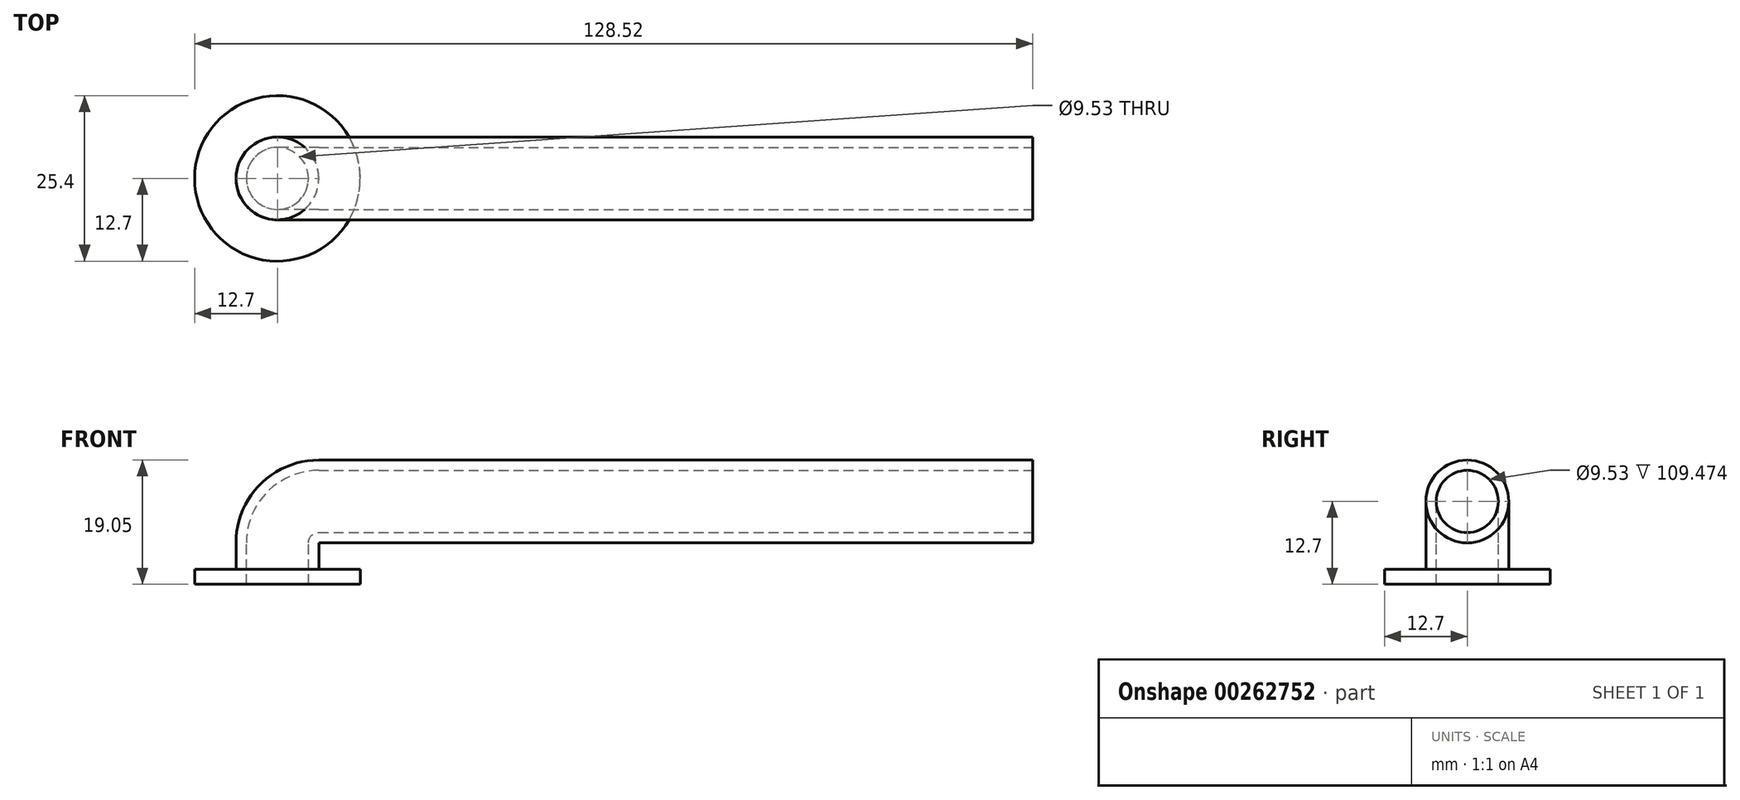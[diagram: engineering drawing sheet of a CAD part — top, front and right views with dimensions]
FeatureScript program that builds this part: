
annotation { "Feature Type Name" : "Feature", "Feature Type Description" : "" }
export const myFeature = defineFeature(function(context is Context, id is Id, definition is map)
    precondition{}
    {
        {
            var Q0;
            Q0=qCreatedBy(makeId("Front.planeOp"),FACE);
            var sketch = newSketch(context, id + "F0", { "sketchPlane" : qUnion([Q0])});
            skLineSegment(sketch, "E0", {"start": v(0, 0) * mm, "end": v(0, 6.35) * mm});
            skLineSegment(sketch, "E1", {"start": v(6.35, 12.7) * mm, "end": v(115.82, 12.7) * mm});
            skPoint(sketch, "E2.visualSharp", {"position": v(0, 12.7) * mm});
            skArc(sketch, "E2.filletArc", {"start": v(6.35, 12.7) * mm, "mid": v(1.86, 10.84) * mm, "end": v(0, 6.35) * mm});
            skSolve(sketch);
        }
        {
            var Q0;
            Q0=qCreatedBy(makeId("Top.planeOp"),FACE);
            var sketch = newSketch(context, id + "F1", { "sketchPlane" : qUnion([Q0])});
            skCircle(sketch, "E3", {"center": v(0, 0) * mm, "radius": 6.35 * mm});
            skCircle(sketch, "E4", {"center": v(0, 0) * mm, "radius": 4.76 * mm});
            skSolve(sketch);
        }
        {
            var Q0;
            Q0=makeQuery(id+"F1.imprint","IMPRINT",FACE,{"disambiguationData":[TD([[makeQuery(id+"F1.imprint","IMPRINT",EDGE,{"derivedFrom":sQuery(id+"F1.wireOp",EDGE,"E3")}),1.0]])]});
            var Q1;
            Q1=sQuery(id+"F0.wireOp",EDGE,"E1");
            var Q2;
            Q2=sQuery(id+"F0.wireOp",EDGE,"E2.filletArc");
            var Q3;
            Q3=sQuery(id+"F0.wireOp",EDGE,"E0");
            sweep(context, id + "F2", {"profiles" : qUnion([Q0]), "path" : qUnion([Q1, Q2, Q3])});
        }
        {
            var Q0;
            Q0=makeQuery(id+"F2.opSweep","CAP_FACE",FACE,{"disambiguationData":[OSD([sQuery(id+"F0.wireOp",VERTEX,"E0.start"),sQuery(id+"F1.wireOp",EDGE,"E3"),sQuery(id+"F1.wireOp",EDGE,"E4")])],"isStart":true});
            var sketch = newSketch(context, id + "F3", { "sketchPlane" : qUnion([Q0])});
            skCircle(sketch, "E5", {"center": v(0, 0) * mm, "radius": 12.7 * mm});
            skSolve(sketch);
        }
        {
            var Q0;
            Q0=makeQuery(id+"F3.imprint","IMPRINT",FACE,{"disambiguationData":[TD([[makeQuery(id+"F3.imprint","IMPRINT",EDGE,{"derivedFrom":sQuery(id+"F3.wireOp",EDGE,"E5")}),1.0]])]});
            var Q1;
            {var subQ0=sQuery(id+"F0.wireOp",VERTEX,"E0.start");Q1=makeQuery(id+"F3.imprint","IMPRINT",FACE,{"disambiguationData":[TD([[makeQuery(id+"F3.imprint","IMPRINT",EDGE,{"derivedFrom":makeQuery(id+"F2.opSweep","CAP_EDGE",EDGE,{"disambiguationData":[OSD([subQ0,sQuery(id+"F1.wireOp",EDGE,"E3")])],"isStart":true})}),-1.0]])]});}
            extrude(context, id + "F4", {"entities" : qUnion([Q0, Q1]), "operationType" : NewBodyOperationType.ADD, "oppositeDirection" : true, "depth" : 2.3 * mm});
        }
    });
